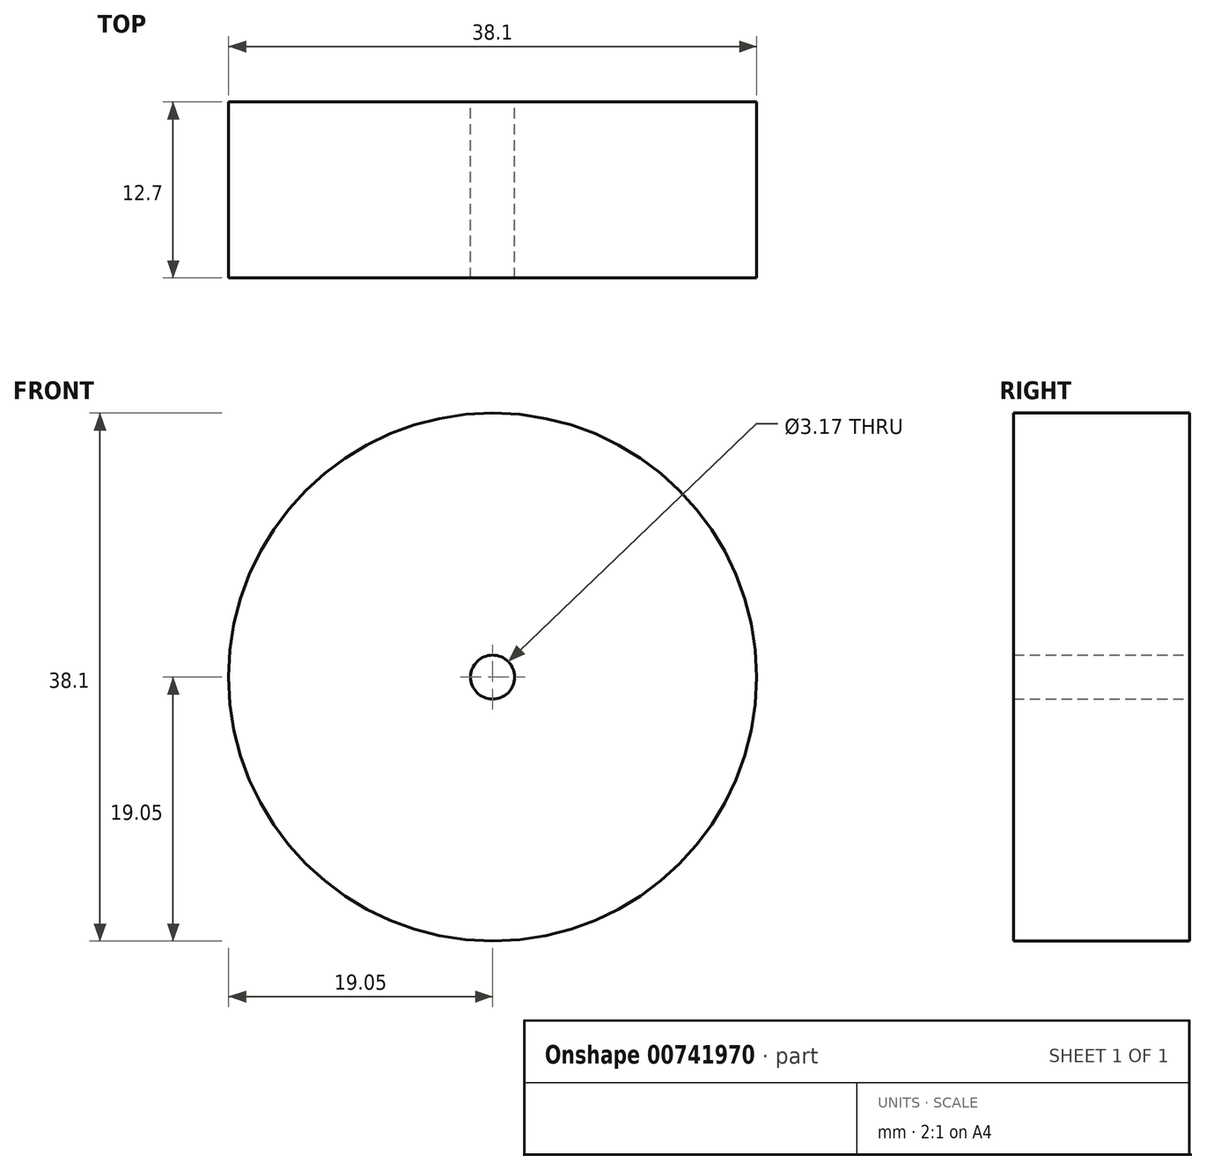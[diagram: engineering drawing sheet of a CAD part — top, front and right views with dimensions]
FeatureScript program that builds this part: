
annotation { "Feature Type Name" : "Feature", "Feature Type Description" : "" }
export const myFeature = defineFeature(function(context is Context, id is Id, definition is map)
    precondition{}
    {
        {
            var Q0;
            Q0=qCreatedBy(makeId("Front.planeOp"),FACE);
            var sketch = newSketch(context, id + "F0", { "sketchPlane" : qUnion([Q0])});
            skCircle(sketch, "E0", {"center": v(0, 0) * mm, "radius": 19.05 * mm});
            skCircle(sketch, "E1", {"center": v(0, 0) * mm, "radius": 1.59 * mm});
            skSolve(sketch);
        }
        {
            var Q0;
            Q0 = qSketchRegion(id + "F0", true);
            extrude(context, id + "F1", {"entities" : qUnion([Q0]), "depth" : 12.7 * mm, "offsetDistance" : 25.4 * mm});
        }
    });
